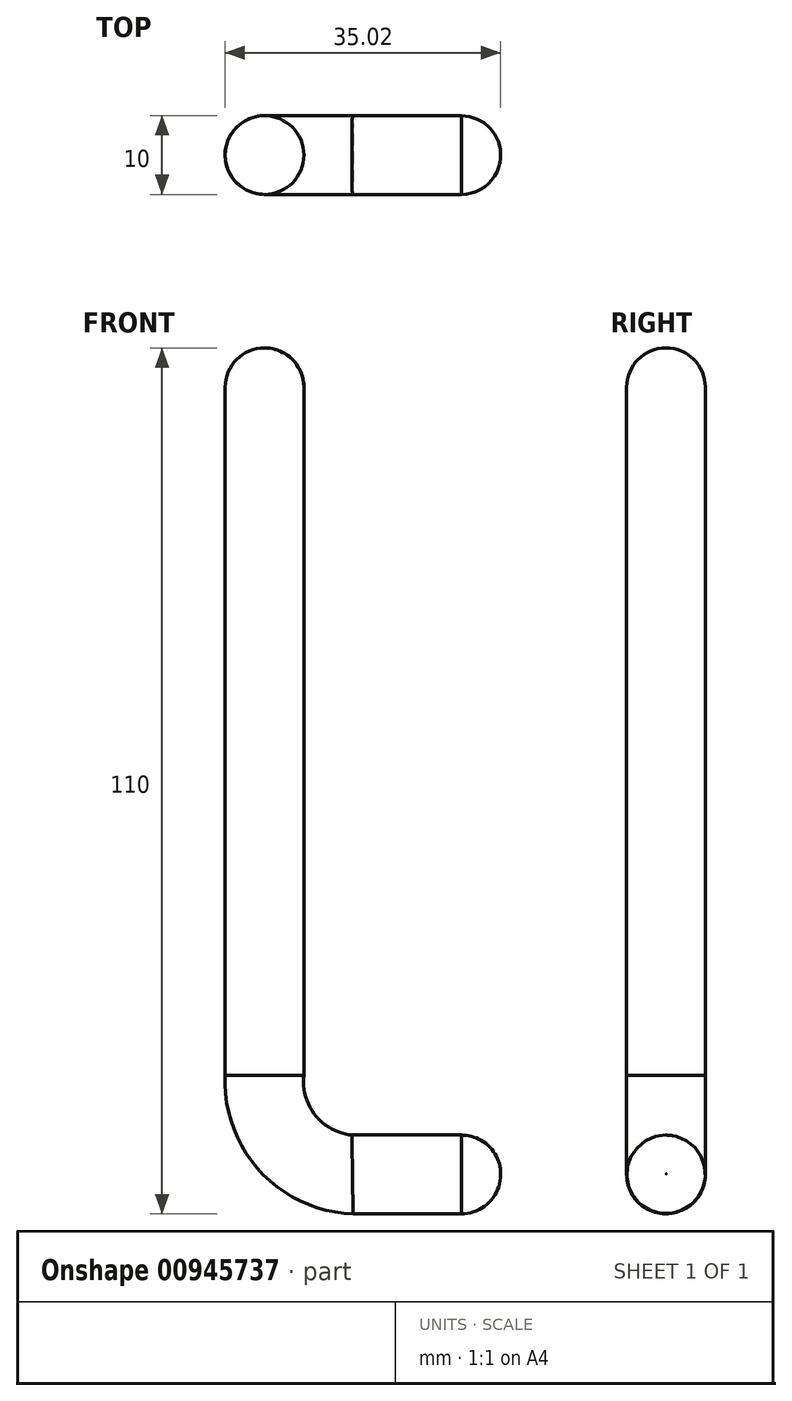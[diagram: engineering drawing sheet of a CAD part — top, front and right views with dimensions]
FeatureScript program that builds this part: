
annotation { "Feature Type Name" : "Feature", "Feature Type Description" : "" }
export const myFeature = defineFeature(function(context is Context, id is Id, definition is map)
    precondition{}
    {
        {
            var Q0;
            Q0=qCreatedBy(makeId("Front.planeOp"),FACE);
            var sketch = newSketch(context, id + "F0", { "sketchPlane" : qUnion([Q0])});
            skLineSegment(sketch, "E0", {"start": v(0, 50) * mm, "end": v(0, -37.42) * mm});
            skLineSegment(sketch, "E1", {"start": v(11.17, -50) * mm, "end": v(30, -50) * mm});
            skArc(sketch, "E2", {"start": v(0, -37.42) * mm, "mid": v(2.95, -46.04) * mm, "end": v(11.17, -50) * mm});
            skPoint(sketch, "E2.first.point", {"position": v(0, -37.42) * mm});
            skPoint(sketch, "E2.second.point", {"position": v(12.4, -50) * mm});
            skPoint(sketch, "E2.third.point", {"position": v(20.06, -29.76) * mm});
            skLineSegment(sketch, "E3", {"start": v(0, 50) * mm, "end": v(0, 55) * mm});
            skSolve(sketch);
        }
        {
            var Q0;
            Q0=qCreatedBy(makeId("Top.planeOp"),FACE);
            var sketch = newSketch(context, id + "F1", { "sketchPlane" : qUnion([Q0])});
            skCircle(sketch, "E4", {"center": v(0, 0) * mm, "radius": 5 * mm});
            skSolve(sketch);
        }
        {
            var Q0;
            Q0=makeQuery(id+"F1.imprint","IMPRINT",FACE,{"disambiguationData":[TD([[makeQuery(id+"F1.imprint","IMPRINT",EDGE,{"derivedFrom":sQuery(id+"F1.wireOp",EDGE,"E4")}),1.0]])]});
            var Q1;
            Q1=sQuery(id+"F0.wireOp",EDGE,"E0");
            var Q2;
            Q2=sQuery(id+"F0.wireOp",EDGE,"E3");
            sweep(context, id + "F2", {"profiles" : qUnion([Q0]), "path" : qUnion([Q1, Q2])});
        }
        {
            var Q0;
            Q0=makeQuery(id+"F2.opSweep","CAP_FACE",FACE,{"disambiguationData":[OSD([sQuery(id+"F0.wireOp",VERTEX,"E0.end"),sQuery(id+"F1.wireOp",EDGE,"E4")])],"isStart":true});
            var Q1;
            Q1=sQuery(id+"F0.wireOp",EDGE,"E2");
            sweep(context, id + "F3", {"operationType" : NewBodyOperationType.ADD, "profiles" : qUnion([Q0]), "path" : qUnion([Q1])});
        }
        {
            var Q0;
            Q0=makeQuery(id+"F3.opSweep","CAP_FACE",FACE,{"disambiguationData":[OSD([sQuery(id+"F0.wireOp",VERTEX,"E0.end"),sQuery(id+"F0.wireOp",VERTEX,"E2.end"),sQuery(id+"F1.wireOp",EDGE,"E4")])],"isStart":false});
            var Q1;
            Q1=sQuery(id+"F0.wireOp",EDGE,"E1");
            var Q2;
            Q2=sQuery(id+"F0.wireOp",EDGE,"krDcuVB1-axmu-uaYu-f4Qy-M67qBNcFj0uM");
            sweep(context, id + "F4", {"operationType" : NewBodyOperationType.ADD, "profiles" : qUnion([Q0]), "path" : qUnion([Q1, Q2])});
        }
        {
            var Q0;
            Q0=makeQuery(id+"F2.opSweep","CAP_EDGE",EDGE,{"disambiguationData":[OSD([sQuery(id+"F0.wireOp",VERTEX,"E3.end"),sQuery(id+"F1.wireOp",EDGE,"E4")])],"isStart":false});
            fillet(context, id + "F5", {"entities" : qUnion([Q0]), "radius" : 5 * mm, "tangentPropagation" : true, "allowEdgeOverflow" : false});
        }
        {
            var Q0;
            Q0=makeQuery(id+"F4.opSweep","CAP_EDGE",EDGE,{"disambiguationData":[OSD([sQuery(id+"F0.wireOp",VERTEX,"E0.end"),sQuery(id+"F0.wireOp",VERTEX,"E1.end"),sQuery(id+"F0.wireOp",VERTEX,"E2.end"),sQuery(id+"F1.wireOp",EDGE,"E4")])],"isStart":false});
            fillet(context, id + "F6", {"entities" : qUnion([Q0]), "radius" : 5 * mm, "tangentPropagation" : true, "allowEdgeOverflow" : false});
        }
    });
